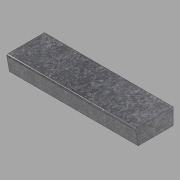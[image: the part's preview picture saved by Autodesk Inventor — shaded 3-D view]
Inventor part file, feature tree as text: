
AUTODESK INVENTOR PART (.ipt)
format: ipt  version: 2022.1 (Build 261234020, 234B)  size: 100,352 bytes
history: native  units: in
note: dims shown in document units (in); Inventor stores cm internally (conversion verified against a paired STEP export)
features: other x3, extrude x1, sketch x1
ambient origin geometry x8: Origin, YZ Plane, XZ Plane, XY Plane, X Axis, Y Axis, Z Axis, Center Point
bodies: Solid1 (feature_tree)
feature tree (5):
  other  "Blocks"
  extrude  "Extrusion1"  Depth=47.75in TaperAngle=0.0deg
  sketch  "Sketch1"  dims[d0=13.0in d1=6.0in d2=13.5in d3=0.5in d4=0.5in d5=47.75in d6=0.0in]
  other  "Profile"
  other  "Profile:1"
